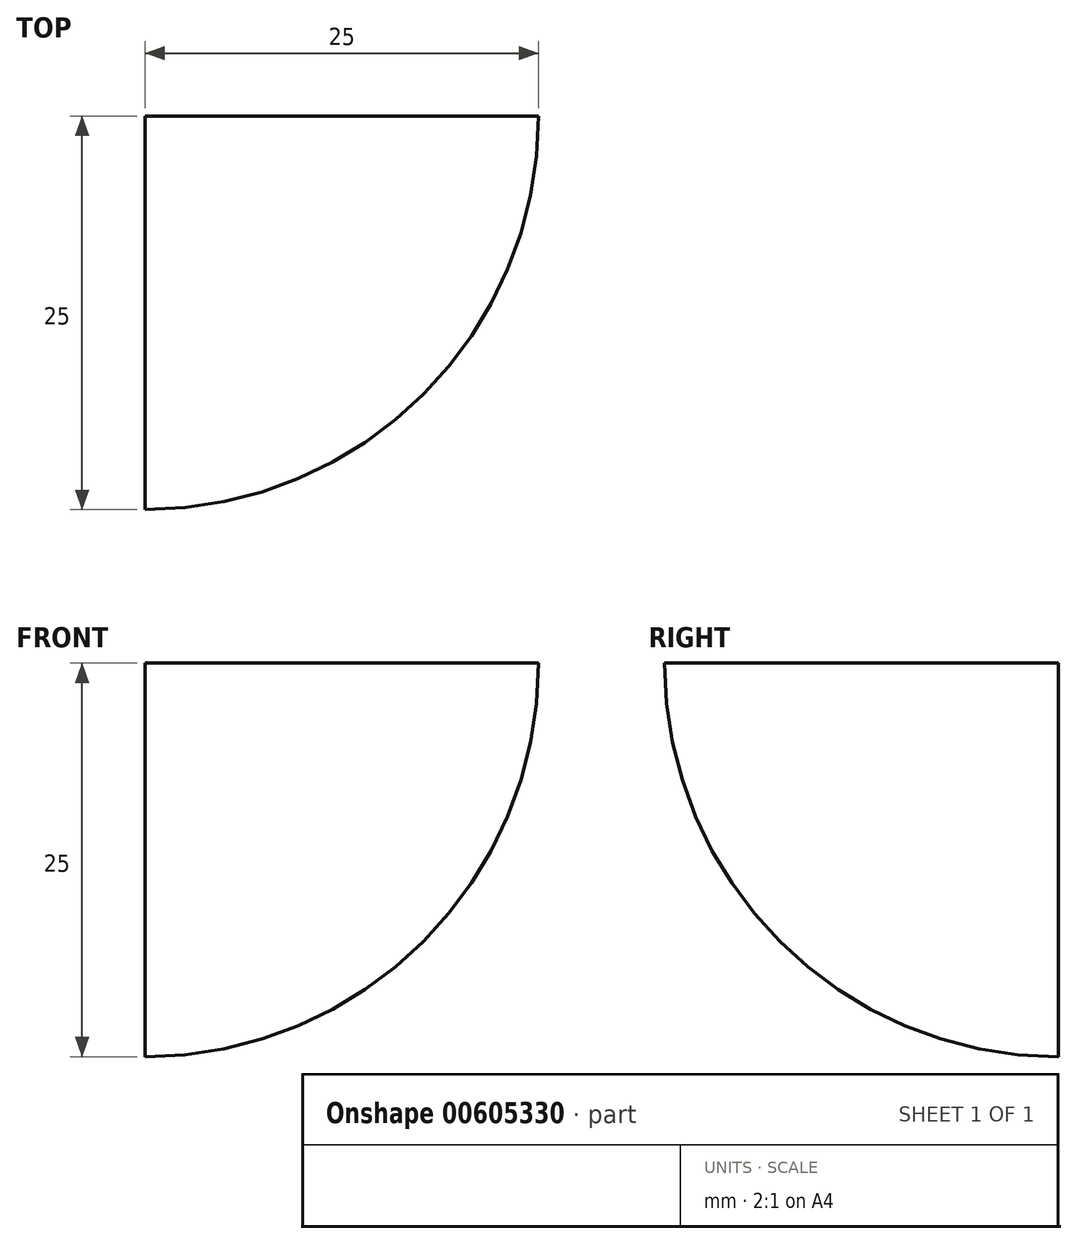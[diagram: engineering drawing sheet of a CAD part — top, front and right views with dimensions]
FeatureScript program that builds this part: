
annotation { "Feature Type Name" : "Feature", "Feature Type Description" : "" }
export const myFeature = defineFeature(function(context is Context, id is Id, definition is map)
    precondition{}
    {
        {
            var Q0;
            Q0=qCreatedBy(makeId("Front.planeOp"),FACE);
            var sketch = newSketch(context, id + "F0", { "sketchPlane" : qUnion([Q0])});
            skArc(sketch, "E0", {"start": v(0, -25) * mm, "mid": v(17.68, -17.68) * mm, "end": v(25, 0) * mm});
            skLineSegment(sketch, "E1", {"start": v(0, 0) * mm, "end": v(25, 0) * mm});
            skLineSegment(sketch, "E2", {"start": v(0, 0) * mm, "end": v(0, -25) * mm});
            skSolve(sketch);
        }
        {
            var Q0;
            Q0 = qSketchRegion(id + "F0", true);
            var Q1;
            Q1=sQuery(id+"F0.wireOp",EDGE,"E2");
            revolve(context, id + "F1", {"entities" : qUnion([Q0]), "axis" : qUnion([Q1]), "revolveType" : RevolveType.ONE_DIRECTION, "angle" : 90 * degree});
        }
    });
